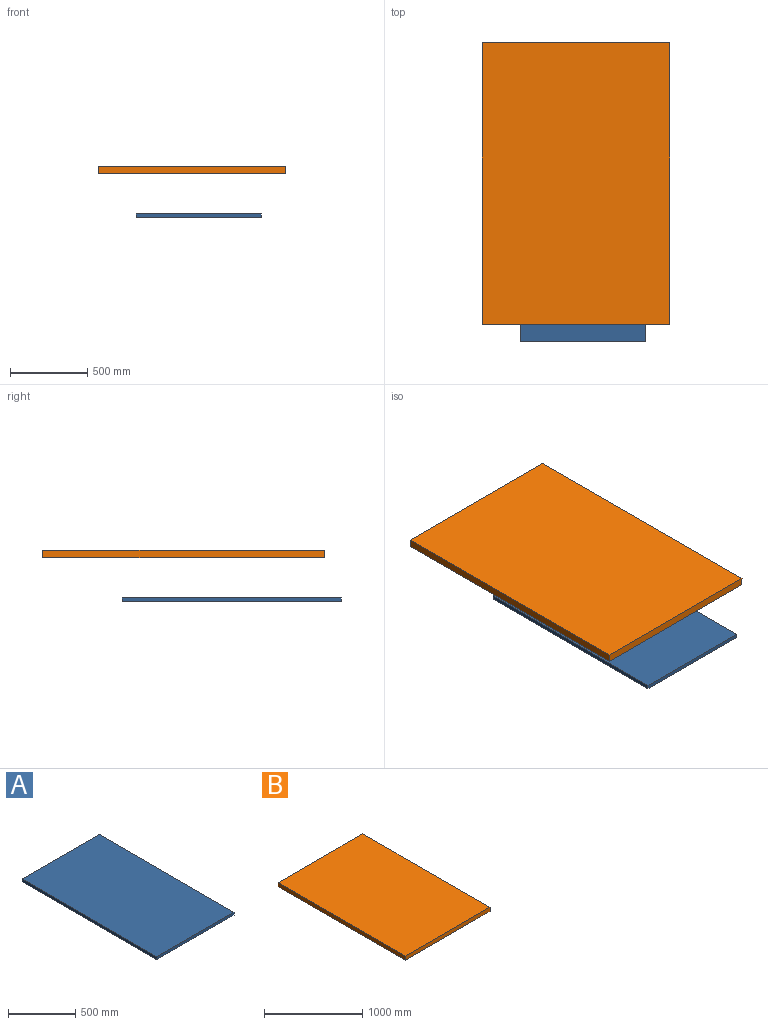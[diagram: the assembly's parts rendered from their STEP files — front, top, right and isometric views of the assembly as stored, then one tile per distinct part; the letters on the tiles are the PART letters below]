
ASSEMBLY  parts=2 mates=1
PART A: 6 faces, bbox 812.8x1422.4x25.4 mm
  f0: plane 812.8x25.4mm, normal (0,-1,0), area 20645.1mm2, adj f1,f3,f4,f5
  f1: plane 1422.4x25.4mm, normal (1,0,0), area 36129mm2, adj f0,f2,f4,f5
  f2: plane 812.8x25.4mm, normal (0,1,0), area 20645.1mm2, adj f1,f3,f4,f5
  f3: plane 1422.4x25.4mm, normal (-1,0,0), area 36129mm2, adj f0,f2,f4,f5
  f4: plane 1422.4x812.8mm, normal (0,0,1), area 1156126.7mm2, adj f0,f1,f2,f3
  f5: plane 1422.4x812.8mm, normal (0,0,-1), area 1156126.7mm2, adj f0,f1,f2,f3
PART B: 6 faces, bbox 1219.2x1828.8x50.8 mm
  f0: plane 1219.2x50.8mm, normal (0,-1,0), area 61935.4mm2, adj f1,f3,f4,f5
  f1: plane 1828.8x50.8mm, normal (1,0,0), area 92903mm2, adj f0,f2,f4,f5
  f2: plane 1219.2x50.8mm, normal (0,1,0), area 61935.4mm2, adj f1,f3,f4,f5
  f3: plane 1828.8x50.8mm, normal (-1,0,0), area 92903mm2, adj f0,f2,f4,f5
  f4: plane 1828.8x1219.2mm, normal (0,0,1), area 2229673mm2, adj f0,f1,f2,f3
  f5: plane 1828.8x1219.2mm, normal (0,0,-1), area 2229673mm2, adj f0,f1,f2,f3
PLACE A t=(4.12,48.01,133.93)mm
PLACE B t=(-39.93,360.13,418.88)mm
MATE parallel B.f0 <-> A.f0  axis (0,-1,0) through (-39.93,-554.27,444.28)mm
